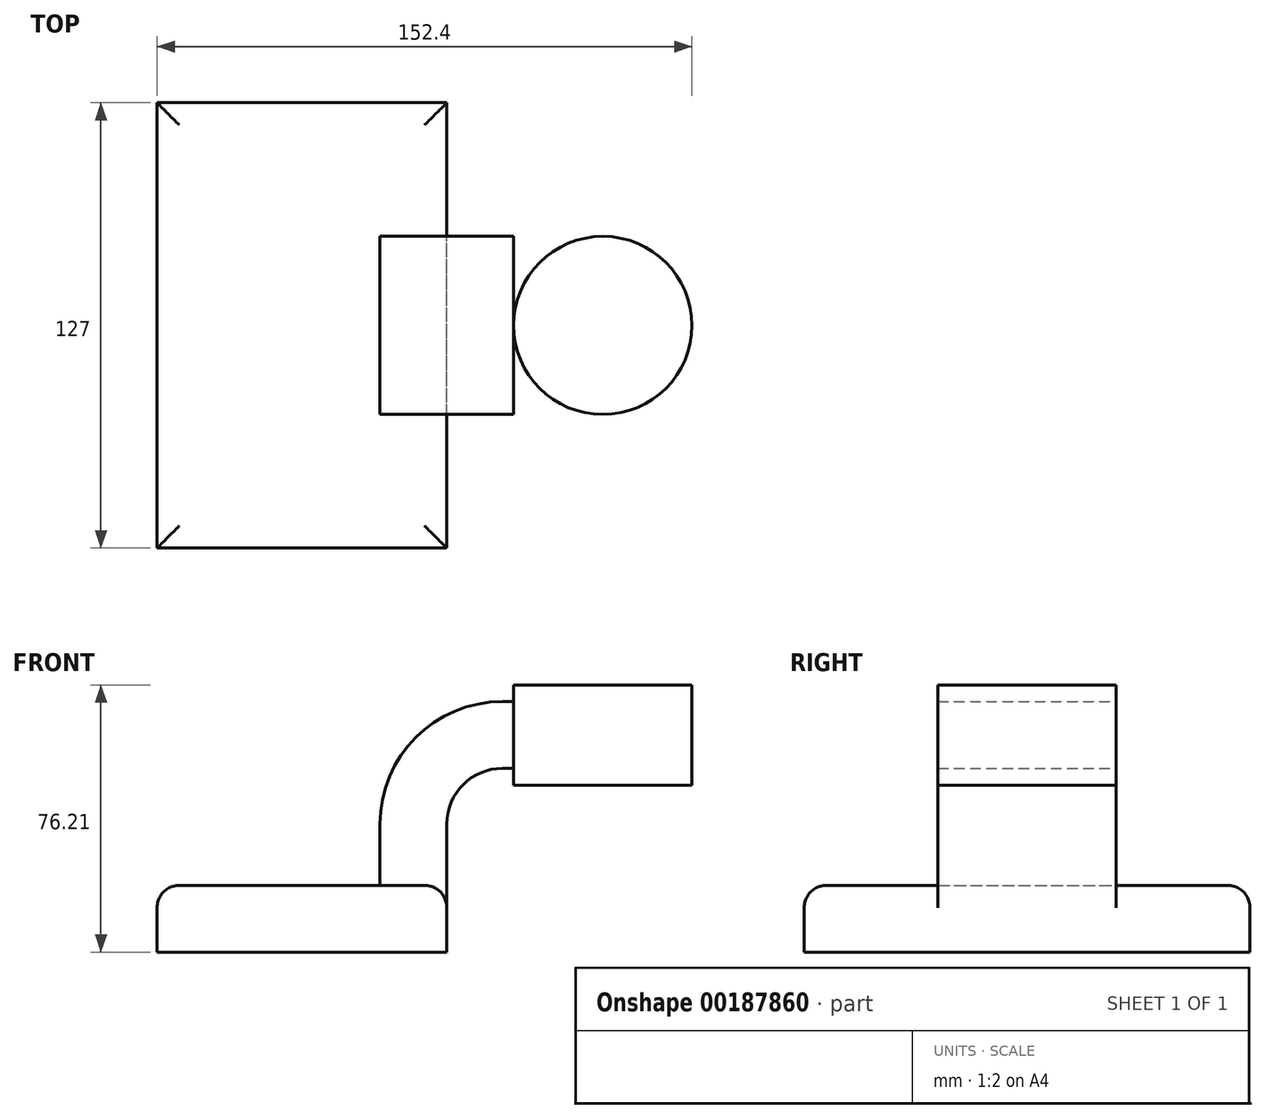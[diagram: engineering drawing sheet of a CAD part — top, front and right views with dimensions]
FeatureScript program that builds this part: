
annotation { "Feature Type Name" : "Feature", "Feature Type Description" : "" }
export const myFeature = defineFeature(function(context is Context, id is Id, definition is map)
    precondition{}
    {
        {
            var Q0;
            Q0=qCreatedBy(makeId("Front.planeOp"),FACE);
            var sketch = newSketch(context, id + "F0", { "sketchPlane" : qUnion([Q0])});
            skLineSegment(sketch, "E0.bottom", {"start": v(41.28, -9.52) * mm, "end": v(-41.28, -9.53) * mm});
            skLineSegment(sketch, "E0.top", {"start": v(41.28, 9.53) * mm, "end": v(-41.28, 9.53) * mm});
            skLineSegment(sketch, "E0.left", {"start": v(41.28, -9.52) * mm, "end": v(41.28, 9.53) * mm});
            skLineSegment(sketch, "E0.right", {"start": v(-41.28, -9.53) * mm, "end": v(-41.28, 9.53) * mm});
            skPoint(sketch, "E0.middle", {"position": v(0, 0) * mm});
            skLineSegment(sketch, "E1.bottom", {"start": v(111.13, 38.1) * mm, "end": v(60.33, 38.1) * mm});
            skLineSegment(sketch, "E1.top", {"start": v(111.13, 66.68) * mm, "end": v(60.33, 66.68) * mm});
            skLineSegment(sketch, "E1.left", {"start": v(111.13, 38.1) * mm, "end": v(111.13, 66.67) * mm});
            skLineSegment(sketch, "E1.right", {"start": v(60.33, 38.1) * mm, "end": v(60.33, 66.67) * mm});
            skPoint(sketch, "E1.middle", {"position": v(85.73, 52.39) * mm});
            skLineSegment(sketch, "E2", {"start": v(41.28, 9.53) * mm, "end": v(41.28, 27) * mm});
            skArc(sketch, "E3", {"start": v(41.27, 27) * mm, "mid": v(45.92, 38.23) * mm, "end": v(57.15, 42.88) * mm});
            skLineSegment(sketch, "E4", {"start": v(57.15, 42.88) * mm, "end": v(85.73, 42.88) * mm});
            skLineSegment(sketch, "E5.0", {"start": v(57.15, 61.93) * mm, "end": v(85.72, 61.93) * mm});
            skArc(sketch, "E5.1", {"start": v(22.23, 27) * mm, "mid": v(32.45, 51.7) * mm, "end": v(57.15, 61.93) * mm});
            skLineSegment(sketch, "E5.2", {"start": v(22.22, 9.53) * mm, "end": v(22.22, 27) * mm});
            skLineSegment(sketch, "E6", {"start": v(85.73, 38.1) * mm, "end": v(85.73, 66.68) * mm});
            skFitSpline(sketch, "E7", {"points": [v(57.15, 61.93) * mm, v(-41.28, 9.53) * mm], "startDerivative": vector(-131.02, 0.21) * mm, "endDerivative": vector(-1.05, -105.19) * mm});
            skSolve(sketch);
        }
        {
            var Q0;
            Q0=makeQuery(id+"F0.imprint","IMPRINT",FACE,{"disambiguationData":[TD([[makeQuery(id+"F0.imprint","IMPRINT",EDGE,{"derivedFrom":sQuery(id+"F0.wireOp",EDGE,"E0.bottom")}),-1.0]])]});
            extrude(context, id + "F1", {"entities" : qUnion([Q0]), "endBound" : BoundingType.SYMMETRIC, "depth" : 127 * mm});
        }
        {
            var Q0;
            {var subQ1=sQuery(id+"F0.wireOp",EDGE,"E2");Q0=makeQuery(id+"F0.imprint","IMPRINT",FACE,{"disambiguationData":[TD([[makeQuery(id+"F0.imprint","IMPRINT",EDGE,{"derivedFrom":subQ1}),1.0]])]});}
            extrude(context, id + "F2", {"entities" : qUnion([Q0]), "operationType" : NewBodyOperationType.ADD, "endBound" : BoundingType.SYMMETRIC, "depth" : 50.8 * mm});
        }
        {
            var Q0;
            Q0=makeQuery(id+"F0.imprint","IMPRINT",FACE,{"disambiguationData":[TD([[makeQuery(id+"F0.imprint","IMPRINT",EDGE,{"derivedFrom":sQuery(id+"F0.wireOp",EDGE,"E5.1")}),1.0]])]});
            extrude(context, id + "F3", {"entities" : qUnion([Q0]), "operationType" : NewBodyOperationType.ADD, "endBound" : BoundingType.SYMMETRIC, "depth" : 15.88 * mm});
        }
        {
            var Q0;
            {var subQ0=sQuery(id+"F0.wireOp",EDGE,"E1.left");Q0=makeQuery(id+"F0.imprint","IMPRINT",FACE,{"disambiguationData":[TD([[makeQuery(id+"F0.imprint","IMPRINT",EDGE,{"derivedFrom":subQ0}),1.0]])]});}
            var Q1;
            Q1=sQuery(id+"F0.wireOp",EDGE,"E6");
            revolve(context, id + "F4", {"operationType" : NewBodyOperationType.ADD, "entities" : qUnion([Q0]), "axis" : qUnion([Q1]), "revolveType" : RevolveType.FULL});
        }
        {
            var Q0;
            {var subQ0=sQuery(id+"F0.wireOp",EDGE,"E7");var subQ1=sQuery(id+"F0.wireOp",EDGE,"E0.top");var subQ2=sQuery(id+"F0.wireOp",EDGE,"E0.right");Q0=makeQuery(id+"F3.boolean.opBoolean","SPLIT",EDGE,{"disambiguationData":[TD([makeQuery(id+"F1.opExtrude","CAP_FACE",FACE,{"disambiguationData":[OSD([sQuery(id+"F0.wireOp",EDGE,"E0.bottom"),subQ1,sQuery(id+"F0.wireOp",EDGE,"E0.left"),subQ2])],"isStart":false})])],"derivedFrom":makeQuery(id+"F1.opExtrude","SWEPT_EDGE",EDGE,{"disambiguationData":[OSD([subQ1,subQ2,subQ0])]})});}
            var Q1;
            Q1=makeQuery(id+"F1.opExtrude","CAP_EDGE",EDGE,{"disambiguationData":[OSD([sQuery(id+"F0.wireOp",EDGE,"E0.top")])],"isStart":false});
            var Q2;
            {var subQ0=sQuery(id+"F0.wireOp",EDGE,"E0.right");var subQ1=sQuery(id+"F0.wireOp",EDGE,"E0.top");var subQ2=sQuery(id+"F0.wireOp",EDGE,"E7");Q2=makeQuery(id+"F3.boolean.opBoolean","SPLIT",EDGE,{"disambiguationData":[TD([makeQuery(id+"F1.opExtrude","CAP_FACE",FACE,{"disambiguationData":[OSD([sQuery(id+"F0.wireOp",EDGE,"E0.bottom"),subQ1,sQuery(id+"F0.wireOp",EDGE,"E0.left"),subQ0])],"isStart":true})])],"derivedFrom":makeQuery(id+"F1.opExtrude","SWEPT_EDGE",EDGE,{"disambiguationData":[OSD([subQ1,subQ0,subQ2])]})});}
            var Q3;
            Q3=makeQuery(id+"F1.opExtrude","CAP_EDGE",EDGE,{"disambiguationData":[OSD([sQuery(id+"F0.wireOp",EDGE,"E0.top")])],"isStart":true});
            var Q4;
            {var subQ0=sQuery(id+"F0.wireOp",EDGE,"E2");var subQ1=sQuery(id+"F0.wireOp",EDGE,"E0.top");var subQ2=sQuery(id+"F0.wireOp",EDGE,"E0.left");Q4=makeQuery(id+"F2.boolean.opBoolean","SPLIT",EDGE,{"disambiguationData":[TD([makeQuery(id+"F1.opExtrude","CAP_FACE",FACE,{"disambiguationData":[OSD([sQuery(id+"F0.wireOp",EDGE,"E0.bottom"),subQ1,subQ2,sQuery(id+"F0.wireOp",EDGE,"E0.right")])],"isStart":true})])],"derivedFrom":makeQuery(id+"F1.opExtrude","SWEPT_EDGE",EDGE,{"disambiguationData":[OSD([subQ1,subQ2,subQ0])]})});}
            var Q5;
            {var subQ0=sQuery(id+"F0.wireOp",EDGE,"E2");var subQ1=sQuery(id+"F0.wireOp",EDGE,"E0.top");var subQ2=sQuery(id+"F0.wireOp",EDGE,"E0.left");Q5=makeQuery(id+"F2.boolean.opBoolean","SPLIT",EDGE,{"disambiguationData":[TD([makeQuery(id+"F1.opExtrude","CAP_FACE",FACE,{"disambiguationData":[OSD([sQuery(id+"F0.wireOp",EDGE,"E0.bottom"),subQ1,subQ2,sQuery(id+"F0.wireOp",EDGE,"E0.right")])],"isStart":false})])],"derivedFrom":makeQuery(id+"F1.opExtrude","SWEPT_EDGE",EDGE,{"disambiguationData":[OSD([subQ1,subQ2,subQ0])]})});}
            fillet(context, id + "F5", {"entities" : qUnion([Q0, Q1, Q2, Q3, Q4, Q5]), "radius" : 6.35 * mm, "tangentPropagation" : true, "allowEdgeOverflow" : false});
        }
    });
